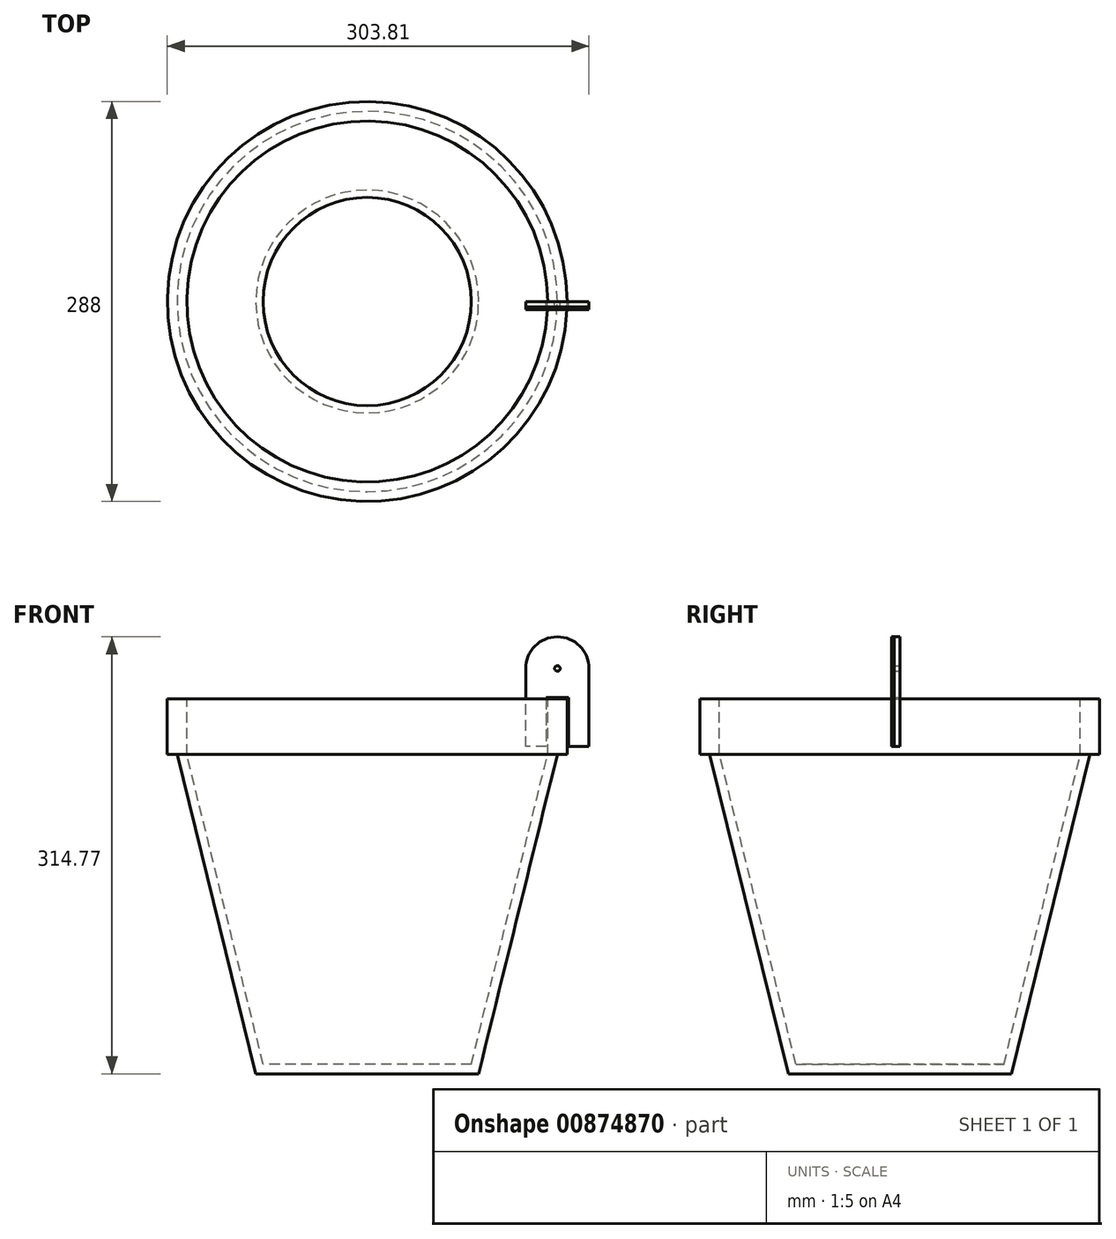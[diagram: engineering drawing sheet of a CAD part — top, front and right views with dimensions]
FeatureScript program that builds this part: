
annotation { "Feature Type Name" : "Feature", "Feature Type Description" : "" }
export const myFeature = defineFeature(function(context is Context, id is Id, definition is map)
    precondition{}
    {
        {
            var Q0;
            Q0=qCreatedBy(makeId("Front.planeOp"),FACE);
            var sketch = newSketch(context, id + "F0", { "sketchPlane" : qUnion([Q0])});
            skLineSegment(sketch, "E0", {"start": v(0, 751.44) * mm, "end": v(0, -783.91) * mm, "construction": true});
            skLineSegment(sketch, "E1", {"start": v(0, -478.36) * mm, "end": v(75, -478.36) * mm});
            skLineSegment(sketch, "E2", {"start": v(75, -478.36) * mm, "end": v(130, -255.36) * mm});
            skLineSegment(sketch, "E3", {"start": v(130, -255.36) * mm, "end": v(144, -255.36) * mm});
            skLineSegment(sketch, "E4", {"start": v(144, -255.36) * mm, "end": v(144, -215.36) * mm});
            skLineSegment(sketch, "E5", {"start": v(144, -215.36) * mm, "end": v(130, -215.36) * mm});
            skLineSegment(sketch, "E6", {"start": v(130, -215.36) * mm, "end": v(130, -255.36) * mm});
            skLineSegment(sketch, "E7", {"start": v(130, -255.36) * mm, "end": v(0, -255.36) * mm, "construction": true});
            skLineSegment(sketch, "E8", {"start": v(137, -255.36) * mm, "end": v(80.27, -485.36) * mm});
            skLineSegment(sketch, "E9", {"start": v(0, -485.36) * mm, "end": v(80.27, -485.36) * mm});
            skLineSegment(sketch, "E10", {"start": v(137, -255.36) * mm, "end": v(130, -255.36) * mm});
            skLineSegment(sketch, "E11", {"start": v(0, -478.36) * mm, "end": v(0, -485.36) * mm});
            skLineSegment(sketch, "E12", {"start": v(145, -249.67) * mm, "end": v(145, -214.36) * mm});
            skLineSegment(sketch, "E13", {"start": v(145, -214.36) * mm, "end": v(129, -214.36) * mm});
            skLineSegment(sketch, "E14", {"start": v(129, -214.36) * mm, "end": v(129, -249.67) * mm});
            skLineSegment(sketch, "E15", {"start": v(129, -249.67) * mm, "end": v(114.2, -249.67) * mm});
            skLineSegment(sketch, "E16", {"start": v(114.2, -249.67) * mm, "end": v(114.2, -193.4) * mm});
            skLineSegment(sketch, "E17", {"start": v(10, 283.25) * mm, "end": v(10, 193.63) * mm});
            skLineSegment(sketch, "E18", {"start": v(10, 193.63) * mm, "end": v(125.28, -173.83) * mm});
            skLineSegment(sketch, "E19", {"start": v(10, 238.44) * mm, "end": v(138.34, -170.63) * mm});
            skLineSegment(sketch, "E20", {"start": v(145, -249.67) * mm, "end": v(159.8, -249.67) * mm});
            skLineSegment(sketch, "E21", {"start": v(159.8, -249.67) * mm, "end": v(159.8, -193.4) * mm});
            skArc(sketch, "E22", {"start": v(159.8, -193.4) * mm, "mid": v(137, -170.6) * mm, "end": v(114.2, -193.4) * mm});
            skCircle(sketch, "E23", {"center": v(137, -193.4) * mm, "radius": 2 * mm});
            skSolve(sketch);
        }
        {
            var Q0;
            Q0=makeQuery(id+"F0.imprint","IMPRINT",FACE,{"disambiguationData":[TD([[makeQuery(id+"F0.imprint","IMPRINT",EDGE,{"derivedFrom":sQuery(id+"F0.wireOp",EDGE,"E1")}),-1.0]])]});
            var Q1;
            Q1=makeQuery(id+"F0.imprint","IMPRINT",FACE,{"disambiguationData":[TD([[makeQuery(id+"F0.imprint","IMPRINT",EDGE,{"derivedFrom":sQuery(id+"F0.wireOp",EDGE,"E3")}),1.0]])]});
            var Q2;
            Q2=sQuery(id+"F0.wireOp",EDGE,"E0");
            revolve(context, id + "F1", {"surfaceOperationType" : NewSurfaceOperationType.NEW, "entities" : qUnion([Q0, Q1]), "axis" : qUnion([Q2]), "revolveType" : RevolveType.FULL});
        }
        {
            var Q0;
            Q0=makeQuery(id+"F0.imprint","IMPRINT",FACE,{"disambiguationData":[TD([[makeQuery(id+"F0.imprint","IMPRINT",EDGE,{"derivedFrom":sQuery(id+"F0.wireOp",EDGE,"E12")}),-1.0]])]});
            extrude(context, id + "F2", {"entities" : qUnion([Q0]), "depth" : 6 * mm, "offsetDistance" : 25 * mm});
        }
        {
            var Q0;
            Q0=makeQuery(id+"F0.imprint","IMPRINT",FACE,{"disambiguationData":[TD([[makeQuery(id+"F0.imprint","IMPRINT",EDGE,{"derivedFrom":sQuery(id+"F0.wireOp",EDGE,"E12")}),-1.0]])]});
            extrude(context, id + "F3", {"entities" : qUnion([Q0]), "depth" : 4 * mm, "offsetDistance" : 25 * mm});
        }
    });
